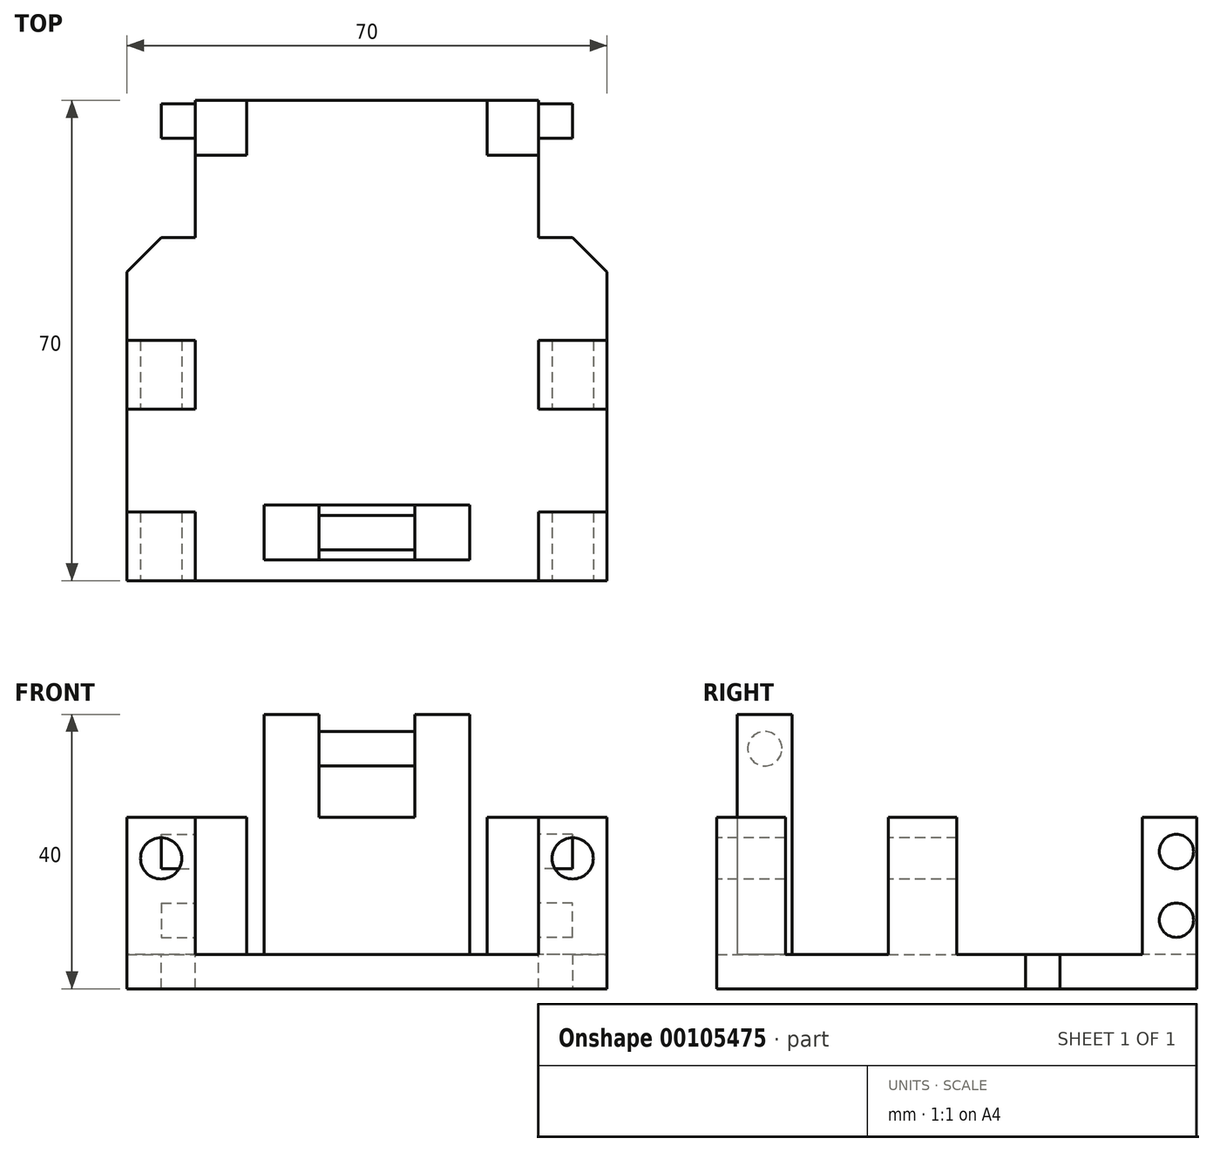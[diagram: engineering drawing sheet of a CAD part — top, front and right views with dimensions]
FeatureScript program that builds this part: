
annotation { "Feature Type Name" : "Feature", "Feature Type Description" : "" }
export const myFeature = defineFeature(function(context is Context, id is Id, definition is map)
    precondition{}
    {
        {
            var Q0;
            Q0=qCreatedBy(makeId("Front.planeOp"),FACE);
            var sketch = newSketch(context, id + "F0", { "sketchPlane" : qUnion([Q0])});
            skLineSegment(sketch, "E0.bottom", {"start": v(25, -10) * mm, "end": v(-25, -10) * mm});
            skLineSegment(sketch, "E0.top", {"start": v(25, 10) * mm, "end": v(-25, 10) * mm});
            skLineSegment(sketch, "E0.left", {"start": v(25, -10) * mm, "end": v(25, 10) * mm});
            skLineSegment(sketch, "E0.right", {"start": v(-25, -10) * mm, "end": v(-25, 10) * mm});
            skPoint(sketch, "E0.middle", {"position": v(0, 0) * mm});
            skSolve(sketch);
        }
        {
            var Q0;
            Q0 = qSketchRegion(id + "F0", true);
            extrude(context, id + "F1", {"entities" : qUnion([Q0]), "depth" : 8 * mm});
        }
        {
            var Q0;
            Q0=makeQuery(id+"F1.opExtrude","SWEPT_FACE",FACE,{"disambiguationData":[OSD([sQuery(id+"F0.wireOp",EDGE,"E0.right")])]});
            var sketch = newSketch(context, id + "F2", { "sketchPlane" : qUnion([Q0])});
            skCircle(sketch, "E1", {"center": v(3, 5) * mm, "radius": 2.5 * mm});
            skCircle(sketch, "E2", {"center": v(3, -5) * mm, "radius": 2.5 * mm});
            skSolve(sketch);
        }
        {
            var Q0;
            Q0 = qSketchRegion(id + "F2", true);
            extrude(context, id + "F3", {"entities" : qUnion([Q0]), "operationType" : NewBodyOperationType.ADD, "depth" : 5 * mm});
        }
        {
            var Q0;
            Q0=makeQuery(id+"F1.opExtrude","SWEPT_FACE",FACE,{"disambiguationData":[OSD([sQuery(id+"F0.wireOp",EDGE,"E0.left")])]});
            var sketch = newSketch(context, id + "F4", { "sketchPlane" : qUnion([Q0])});
            skCircle(sketch, "E3", {"center": v(-3, 5) * mm, "radius": 2.5 * mm});
            skCircle(sketch, "E4", {"center": v(-3, -5) * mm, "radius": 2.5 * mm});
            skSolve(sketch);
        }
        {
            var Q0;
            Q0 = qSketchRegion(id + "F4", true);
            extrude(context, id + "F5", {"entities" : qUnion([Q0]), "operationType" : NewBodyOperationType.ADD, "depth" : 5 * mm});
        }
        {
            var Q0;
            Q0=makeQuery(id+"F1.opExtrude","CAP_FACE",FACE,{"disambiguationData":[OSD([sQuery(id+"F0.wireOp",EDGE,"E0.bottom"),sQuery(id+"F0.wireOp",EDGE,"E0.top"),sQuery(id+"F0.wireOp",EDGE,"E0.left"),sQuery(id+"F0.wireOp",EDGE,"E0.right")])],"isStart":false});
            var sketch = newSketch(context, id + "F6", { "sketchPlane" : qUnion([Q0])});
            skLineSegment(sketch, "E5.bottom", {"start": v(-17.5, 20) * mm, "end": v(17.5, 20) * mm});
            skLineSegment(sketch, "E5.top", {"start": v(-17.5, -10) * mm, "end": v(17.5, -10) * mm});
            skLineSegment(sketch, "E5.left", {"start": v(-17.5, 20) * mm, "end": v(-17.5, -10) * mm});
            skLineSegment(sketch, "E5.right", {"start": v(17.5, 20) * mm, "end": v(17.5, -10) * mm});
            skSolve(sketch);
        }
        {
            var Q0;
            Q0 = qSketchRegion(id + "F6", true);
            extrude(context, id + "F7", {"entities" : qUnion([Q0]), "operationType" : NewBodyOperationType.REMOVE, "oppositeDirection" : true, "depth" : 25 * mm});
        }
        {
            var Q0;
            Q0=makeQuery(id+"F1.opExtrude","SWEPT_FACE",FACE,{"disambiguationData":[OSD([sQuery(id+"F0.wireOp",EDGE,"E0.bottom")])]});
            var sketch = newSketch(context, id + "F8", { "sketchPlane" : qUnion([Q0])});
            skLineSegment(sketch, "E6.bottom", {"start": v(-25, 0) * mm, "end": v(25, 0) * mm});
            skLineSegment(sketch, "E6.left", {"start": v(-25, 0) * mm, "end": v(-25, 20) * mm});
            skLineSegment(sketch, "E6.right", {"start": v(25, 0) * mm, "end": v(25, 20) * mm});
            skLineSegment(sketch, "E7.top", {"start": v(35, 20) * mm, "end": v(25, 20) * mm});
            skLineSegment(sketch, "E7.left", {"start": v(35, 70) * mm, "end": v(35, 20) * mm});
            skLineSegment(sketch, "E7.right", {"start": v(-35, 70) * mm, "end": v(-35, 20) * mm});
            skPoint(sketch, "E7.middle", {"position": v(0, 45) * mm});
            skLineSegment(sketch, "E8.trimOffspring", {"start": v(-25, 20) * mm, "end": v(-35, 20) * mm});
            skLineSegment(sketch, "E9", {"start": v(-35, 70) * mm, "end": v(35, 70) * mm});
            skSolve(sketch);
        }
        {
            var Q0;
            Q0 = qSketchRegion(id + "F8", true);
            extrude(context, id + "F9", {"entities" : qUnion([Q0]), "operationType" : NewBodyOperationType.ADD, "depth" : 5 * mm});
        }
        {
            var Q0;
            Q0=makeQuery(id+"F9.opExtrude","CAP_FACE",FACE,{"disambiguationData":[OSD([sQuery(id+"F8.wireOp",EDGE,"E6.bottom"),sQuery(id+"F8.wireOp",EDGE,"E6.left"),sQuery(id+"F8.wireOp",EDGE,"E6.right"),sQuery(id+"F8.wireOp",EDGE,"E7.top"),sQuery(id+"F8.wireOp",EDGE,"E7.left"),sQuery(id+"F8.wireOp",EDGE,"E7.right"),sQuery(id+"F8.wireOp",EDGE,"E8.trimOffspring"),sQuery(id+"F8.wireOp",EDGE,"E9")])],"isStart":true});
            var sketch = newSketch(context, id + "F10", { "sketchPlane" : qUnion([Q0])});
            skLineSegment(sketch, "E10.bottom", {"start": v(-15, -59) * mm, "end": v(-7, -59) * mm});
            skLineSegment(sketch, "E10.top", {"start": v(-15, -67) * mm, "end": v(-7, -67) * mm});
            skLineSegment(sketch, "E10.left", {"start": v(-15, -59) * mm, "end": v(-15, -67) * mm});
            skLineSegment(sketch, "E10.right", {"start": v(-7, -59) * mm, "end": v(-7, -67) * mm});
            skLineSegment(sketch, "E11.bottom", {"start": v(7, -59) * mm, "end": v(15, -59) * mm});
            skLineSegment(sketch, "E11.top", {"start": v(7, -67) * mm, "end": v(15, -67) * mm});
            skLineSegment(sketch, "E11.left", {"start": v(7, -59) * mm, "end": v(7, -67) * mm});
            skLineSegment(sketch, "E11.right", {"start": v(15, -59) * mm, "end": v(15, -67) * mm});
            skSolve(sketch);
        }
        {
            var Q0;
            Q0 = qSketchRegion(id + "F10", true);
            extrude(context, id + "F11", {"entities" : qUnion([Q0]), "operationType" : NewBodyOperationType.ADD, "depth" : 35 * mm});
        }
        {
            var Q0;
            Q0=makeQuery(id+"F11.opExtrude","SWEPT_FACE",FACE,{"disambiguationData":[OSD([sQuery(id+"F10.wireOp",EDGE,"E11.left")])]});
            var sketch = newSketch(context, id + "F12", { "sketchPlane" : qUnion([Q0])});
            skPoint(sketch, "E12.centerSnap0", {"position": v(63, 25) * mm});
            skCircle(sketch, "E13", {"center": v(63, 20) * mm, "radius": 2.5 * mm});
            skSolve(sketch);
        }
        {
            var Q0;
            Q0 = qSketchRegion(id + "F12", true);
            var Q1;
            Q1=makeQuery(id+"F11.opExtrude","SWEPT_FACE",FACE,{"disambiguationData":[OSD([sQuery(id+"F10.wireOp",EDGE,"E10.right")])]});
            extrude(context, id + "F13", {"entities" : qUnion([Q0]), "operationType" : NewBodyOperationType.ADD, "endBound" : BoundingType.UP_TO_SURFACE, "endBoundEntityFace" : qUnion([Q1]), "depth" : 25 * mm});
        }
        {
            var Q0;
            Q0=makeQuery(id+"F9.opExtrude","CAP_FACE",FACE,{"disambiguationData":[OSD([sQuery(id+"F8.wireOp",EDGE,"E6.bottom"),sQuery(id+"F8.wireOp",EDGE,"E6.left"),sQuery(id+"F8.wireOp",EDGE,"E6.right"),sQuery(id+"F8.wireOp",EDGE,"E7.top"),sQuery(id+"F8.wireOp",EDGE,"E7.left"),sQuery(id+"F8.wireOp",EDGE,"E7.right"),sQuery(id+"F8.wireOp",EDGE,"E8.trimOffspring"),sQuery(id+"F8.wireOp",EDGE,"E9")])],"isStart":true});
            var sketch = newSketch(context, id + "F14", { "sketchPlane" : qUnion([Q0])});
            skLineSegment(sketch, "E14.bottom", {"start": v(-35, -70) * mm, "end": v(-25, -70) * mm});
            skLineSegment(sketch, "E14.top", {"start": v(-35, -60) * mm, "end": v(-25, -60) * mm});
            skLineSegment(sketch, "E14.left", {"start": v(-35, -70) * mm, "end": v(-35, -60) * mm});
            skLineSegment(sketch, "E14.right", {"start": v(-25, -70) * mm, "end": v(-25, -60) * mm});
            skLineSegment(sketch, "E15.bottom", {"start": v(35, -70) * mm, "end": v(25, -70) * mm});
            skLineSegment(sketch, "E15.top", {"start": v(35, -60) * mm, "end": v(25, -60) * mm});
            skLineSegment(sketch, "E15.left", {"start": v(35, -70) * mm, "end": v(35, -60) * mm});
            skLineSegment(sketch, "E15.right", {"start": v(25, -70) * mm, "end": v(25, -60) * mm});
            skLineSegment(sketch, "E16.bottom", {"start": v(35, -45) * mm, "end": v(25, -45) * mm});
            skLineSegment(sketch, "E16.top", {"start": v(35, -35) * mm, "end": v(25, -35) * mm});
            skLineSegment(sketch, "E16.left", {"start": v(35, -45) * mm, "end": v(35, -35) * mm});
            skLineSegment(sketch, "E16.right", {"start": v(25, -45) * mm, "end": v(25, -35) * mm});
            skPoint(sketch, "E17.oppositeSnap0", {"position": v(-25, -65) * mm});
            skLineSegment(sketch, "E17.bottom", {"start": v(-35, -45) * mm, "end": v(-25, -45) * mm});
            skLineSegment(sketch, "E17.top", {"start": v(-35, -35) * mm, "end": v(-25, -35) * mm});
            skLineSegment(sketch, "E17.left", {"start": v(-35, -45) * mm, "end": v(-35, -35) * mm});
            skLineSegment(sketch, "E17.right", {"start": v(-25, -45) * mm, "end": v(-25, -35) * mm});
            skSolve(sketch);
        }
        {
            var Q0;
            Q0 = qSketchRegion(id + "F14", true);
            extrude(context, id + "F15", {"entities" : qUnion([Q0]), "operationType" : NewBodyOperationType.ADD, "depth" : 20 * mm});
        }
        {
            var Q0;
            Q0=makeQuery(id+"F15.boolean.opBoolean","MERGE",FACE,{"derivedFrom":[makeQuery(id+"F9.opExtrude","SWEPT_FACE",FACE,{"disambiguationData":[OSD([sQuery(id+"F8.wireOp",EDGE,"E9")])]}),makeQuery(id+"F15.opExtrude","SWEPT_FACE",FACE,{"disambiguationData":[OSD([sQuery(id+"F14.wireOp",EDGE,"E14.bottom")])]}),makeQuery(id+"F15.opExtrude","SWEPT_FACE",FACE,{"disambiguationData":[OSD([sQuery(id+"F14.wireOp",EDGE,"E15.bottom")])]})]});
            var sketch = newSketch(context, id + "F16", { "sketchPlane" : qUnion([Q0])});
            skCircle(sketch, "E18", {"center": v(30, 4) * mm, "radius": 3 * mm});
            skPoint(sketch, "E18.centerSnap0", {"position": v(30, 10) * mm});
            skCircle(sketch, "E19", {"center": v(-30, 4) * mm, "radius": 3 * mm});
            skPoint(sketch, "E19.centerSnap0", {"position": v(-30, 10) * mm});
            skSolve(sketch);
        }
        {
            var Q0;
            Q0 = qSketchRegion(id + "F16", true);
            extrude(context, id + "F17", {"entities" : qUnion([Q0]), "operationType" : NewBodyOperationType.REMOVE, "oppositeDirection" : true, "depth" : 50 * mm});
        }
        {
            var Q0;
            Q0=makeQuery(id+"F9.opExtrude","SWEPT_EDGE",EDGE,{"disambiguationData":[OSD([sQuery(id+"F8.wireOp",EDGE,"E7.right"),sQuery(id+"F8.wireOp",EDGE,"E8.trimOffspring")])]});
            chamfer(context, id + "F18", {"entities" : qUnion([Q0]), "width" : 5 * mm, "tangentPropagation" : true});
        }
        {
            var Q0;
            Q0=makeQuery(id+"F9.opExtrude","SWEPT_EDGE",EDGE,{"disambiguationData":[OSD([sQuery(id+"F8.wireOp",EDGE,"E7.top"),sQuery(id+"F8.wireOp",EDGE,"E7.left")])]});
            chamfer(context, id + "F19", {"entities" : qUnion([Q0]), "width" : 5 * mm, "tangentPropagation" : true});
        }
        {
            var Q0;
            Q0=makeQuery(id+"F9.opExtrude","CAP_FACE",FACE,{"disambiguationData":[OSD([sQuery(id+"F8.wireOp",EDGE,"E6.bottom"),sQuery(id+"F8.wireOp",EDGE,"E6.left"),sQuery(id+"F8.wireOp",EDGE,"E6.right"),sQuery(id+"F8.wireOp",EDGE,"E7.top"),sQuery(id+"F8.wireOp",EDGE,"E7.left"),sQuery(id+"F8.wireOp",EDGE,"E7.right"),sQuery(id+"F8.wireOp",EDGE,"E8.trimOffspring"),sQuery(id+"F8.wireOp",EDGE,"E9")])],"isStart":true});
            var sketch = newSketch(context, id + "F20", { "sketchPlane" : qUnion([Q0])});
            skLineSegment(sketch, "E20.bottom", {"start": v(-7, -59) * mm, "end": v(7, -59) * mm});
            skLineSegment(sketch, "E20.top", {"start": v(-7, -67) * mm, "end": v(7, -67) * mm});
            skLineSegment(sketch, "E20.left", {"start": v(-7, -59) * mm, "end": v(-7, -67) * mm});
            skLineSegment(sketch, "E20.right", {"start": v(7, -59) * mm, "end": v(7, -67) * mm});
            skSolve(sketch);
        }
        {
            var Q0;
            Q0 = qSketchRegion(id + "F20", true);
            extrude(context, id + "F21", {"entities" : qUnion([Q0]), "operationType" : NewBodyOperationType.ADD, "depth" : 20 * mm});
        }
    });
